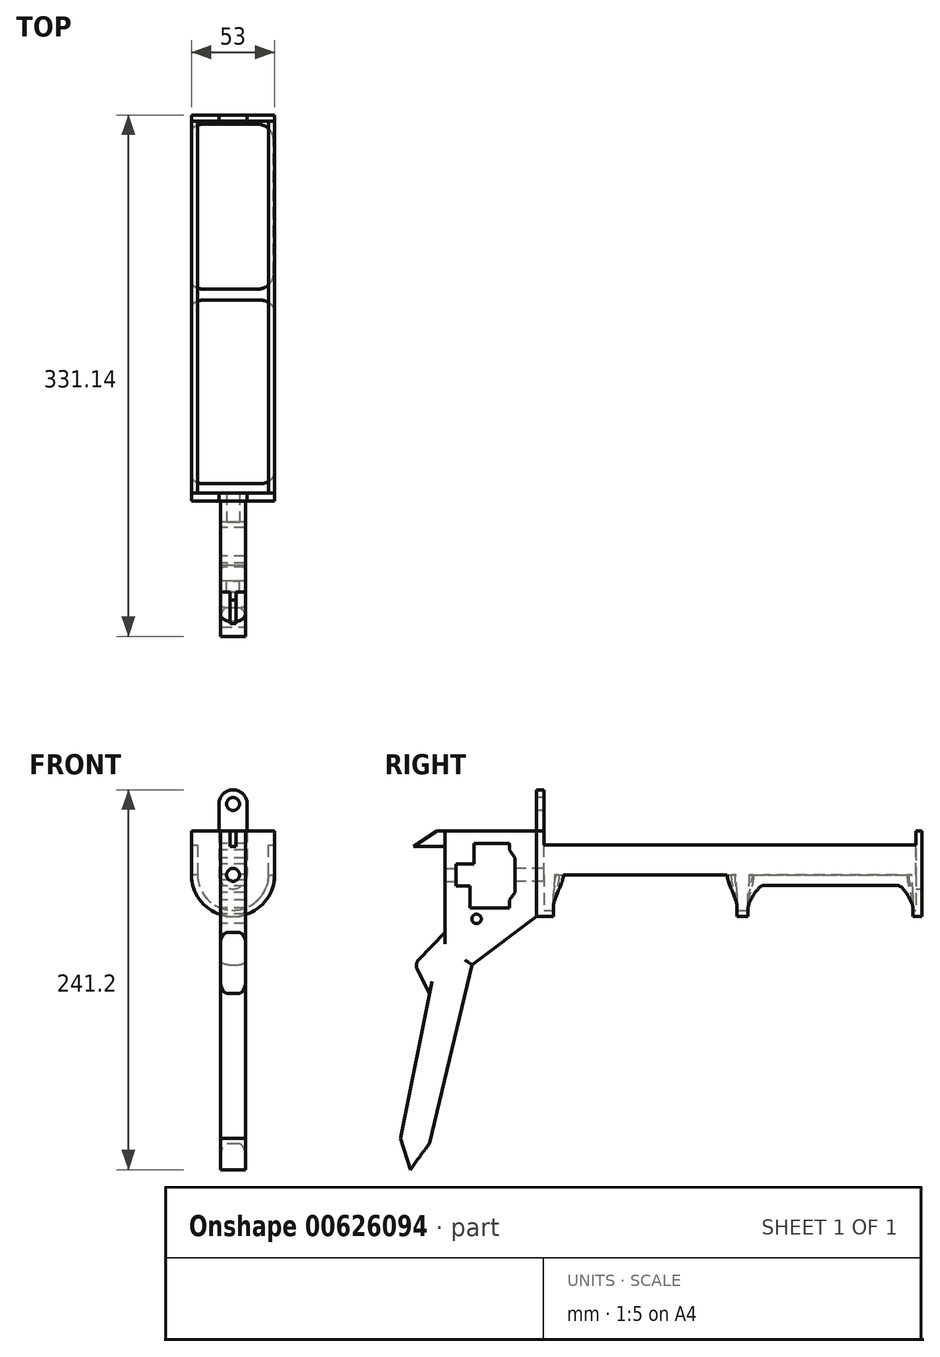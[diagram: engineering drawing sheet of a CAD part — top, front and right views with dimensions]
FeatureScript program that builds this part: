
annotation { "Feature Type Name" : "Feature", "Feature Type Description" : "" }
export const myFeature = defineFeature(function(context is Context, id is Id, definition is map)
    precondition{}
    {
        {
            var Q0;
            Q0=qCreatedBy(makeId("Front.planeOp"),FACE);
            var sketch = newSketch(context, id + "F0", { "sketchPlane" : qUnion([Q0])});
            skLineSegment(sketch, "E0", {"start": v(-22.5, 19) * mm, "end": v(-22.5, 0) * mm});
            skLineSegment(sketch, "E1", {"start": v(22.5, 0) * mm, "end": v(22.5, 19) * mm});
            skArc(sketch, "E2", {"start": v(-22.5, 0) * mm, "mid": v(0, -22.5) * mm, "end": v(22.5, 0) * mm});
            skLineSegment(sketch, "E3", {"start": v(-26.5, 19) * mm, "end": v(-26.5, 0) * mm});
            skLineSegment(sketch, "E4", {"start": v(26.5, 19) * mm, "end": v(26.5, 0) * mm});
            skArc(sketch, "E5", {"start": v(-26.5, 0) * mm, "mid": v(0, -26.5) * mm, "end": v(26.5, 0) * mm});
            skLineSegment(sketch, "E6", {"start": v(-26.5, 19) * mm, "end": v(-22.5, 19) * mm});
            skLineSegment(sketch, "E7", {"start": v(22.5, 19) * mm, "end": v(26.5, 19) * mm});
            skSolve(sketch);
        }
        {
            var Q0;
            Q0=makeQuery(id+"F0.imprint","IMPRINT",FACE,{"disambiguationData":[TD([[makeQuery(id+"F0.imprint","IMPRINT",EDGE,{"derivedFrom":sQuery(id+"F0.wireOp",EDGE,"E0")}),-1.0]])]});
            extrude(context, id + "F1", {"entities" : qUnion([Q0]), "depth" : 245 * mm, "offsetDistance" : 25 * mm});
        }
        {
            var Q0;
            Q0=qCreatedBy(makeId("Top.planeOp"),FACE);
            var sketch = newSketch(context, id + "F2", { "sketchPlane" : qUnion([Q0])});
            skLineSegment(sketch, "E8.bottom", {"start": v(-18.87, -5.77) * mm, "end": v(15.64, -5.77) * mm});
            skLineSegment(sketch, "E8.top", {"start": v(-18.87, -110.54) * mm, "end": v(15.64, -110.54) * mm});
            skLineSegment(sketch, "E8.left", {"start": v(-28.87, -15.77) * mm, "end": v(-28.87, -100.54) * mm});
            skLineSegment(sketch, "E8.right", {"start": v(25.64, -15.77) * mm, "end": v(25.64, -100.54) * mm});
            skLineSegment(sketch, "E9.bottom", {"start": v(-18.87, -117.53) * mm, "end": v(17.22, -117.53) * mm});
            skLineSegment(sketch, "E9.top", {"start": v(-18.87, -234.13) * mm, "end": v(17.22, -234.13) * mm});
            skLineSegment(sketch, "E9.left", {"start": v(-28.87, -127.53) * mm, "end": v(-28.87, -224.13) * mm});
            skLineSegment(sketch, "E9.right", {"start": v(27.22, -127.53) * mm, "end": v(27.22, -224.13) * mm});
            skPoint(sketch, "E10.visualSharp", {"position": v(-28.87, -117.53) * mm});
            skArc(sketch, "E10.filletArc", {"start": v(-18.87, -117.53) * mm, "mid": v(-25.94, -120.46) * mm, "end": v(-28.87, -127.53) * mm});
            skPoint(sketch, "E11.visualSharp", {"position": v(27.22, -117.53) * mm});
            skArc(sketch, "E11.filletArc", {"start": v(27.22, -127.53) * mm, "mid": v(24.3, -120.46) * mm, "end": v(17.22, -117.53) * mm});
            skPoint(sketch, "E12.visualSharp", {"position": v(-28.87, -234.13) * mm});
            skArc(sketch, "E12.filletArc", {"start": v(-28.87, -224.13) * mm, "mid": v(-25.94, -231.2) * mm, "end": v(-18.87, -234.13) * mm});
            skPoint(sketch, "E13.visualSharp", {"position": v(27.22, -234.13) * mm});
            skArc(sketch, "E13.filletArc", {"start": v(17.22, -234.13) * mm, "mid": v(24.3, -231.2) * mm, "end": v(27.22, -224.13) * mm});
            skPoint(sketch, "E14.visualSharp", {"position": v(-28.87, -110.54) * mm});
            skArc(sketch, "E14.filletArc", {"start": v(-28.87, -100.54) * mm, "mid": v(-25.94, -107.61) * mm, "end": v(-18.87, -110.54) * mm});
            skPoint(sketch, "E15.visualSharp", {"position": v(25.64, -110.54) * mm});
            skArc(sketch, "E15.filletArc", {"start": v(15.64, -110.54) * mm, "mid": v(22.72, -107.61) * mm, "end": v(25.64, -100.54) * mm});
            skPoint(sketch, "E16.visualSharp", {"position": v(25.64, -5.77) * mm});
            skArc(sketch, "E16.filletArc", {"start": v(25.64, -15.77) * mm, "mid": v(22.72, -8.7) * mm, "end": v(15.64, -5.77) * mm});
            skPoint(sketch, "E17.visualSharp", {"position": v(-28.87, -5.77) * mm});
            skArc(sketch, "E17.filletArc", {"start": v(-18.87, -5.77) * mm, "mid": v(-25.94, -8.7) * mm, "end": v(-28.87, -15.77) * mm});
            skSolve(sketch);
        }
        {
            var Q0;
            Q0=makeQuery(id+"F2.imprint","IMPRINT",FACE,{"disambiguationData":[TD([[makeQuery(id+"F2.imprint","IMPRINT",EDGE,{"derivedFrom":sQuery(id+"F2.wireOp",EDGE,"E9.bottom")}),-1.0]])]});
            var Q1;
            Q1=makeQuery(id+"F2.imprint","IMPRINT",FACE,{"disambiguationData":[TD([[makeQuery(id+"F2.imprint","IMPRINT",EDGE,{"derivedFrom":sQuery(id+"F2.wireOp",EDGE,"E8.bottom")}),-1.0]])]});
            extrude(context, id + "F3", {"entities" : qUnion([Q0, Q1]), "operationType" : NewBodyOperationType.REMOVE, "endBound" : BoundingType.THROUGH_ALL, "oppositeDirection" : true, "depth" : 25 * mm, "offsetDistance" : 25 * mm});
        }
        {
            var Q0;
            Q0=makeQuery(id+"F1.opExtrude","CAP_FACE",FACE,{"disambiguationData":[OSD([sQuery(id+"F0.wireOp",EDGE,"E0"),sQuery(id+"F0.wireOp",EDGE,"E1"),sQuery(id+"F0.wireOp",EDGE,"E2"),sQuery(id+"F0.wireOp",EDGE,"E3"),sQuery(id+"F0.wireOp",EDGE,"E4"),sQuery(id+"F0.wireOp",EDGE,"E5"),sQuery(id+"F0.wireOp",EDGE,"E6"),sQuery(id+"F0.wireOp",EDGE,"E7")])],"isStart":true});
            var sketch = newSketch(context, id + "F4", { "sketchPlane" : qUnion([Q0])});
            skLineSegment(sketch, "E18", {"start": v(-22.5, 19) * mm, "end": v(-8.92, 19) * mm});
            skLineSegment(sketch, "E19", {"start": v(-8.92, 19) * mm, "end": v(-8.92, 0) * mm});
            skLineSegment(sketch, "E20", {"start": v(22.5, 19) * mm, "end": v(8.92, 19) * mm});
            skLineSegment(sketch, "E21", {"start": v(8.92, 19) * mm, "end": v(8.92, 0) * mm});
            skArc(sketch, "E22", {"start": v(-8.92, 0) * mm, "mid": v(0, -8.92) * mm, "end": v(8.92, 0) * mm});
            skSolve(sketch);
        }
        {
            var Q0;
            Q0=makeQuery(id+"F4.imprint","IMPRINT",FACE,{"disambiguationData":[TD([[makeQuery(id+"F4.imprint","IMPRINT",EDGE,{"derivedFrom":sQuery(id+"F4.wireOp",EDGE,"E18")}),-1.0]])]});
            extrude(context, id + "F5", {"entities" : qUnion([Q0]), "operationType" : NewBodyOperationType.ADD, "oppositeDirection" : true, "depth" : 4 * mm, "offsetDistance" : 25 * mm});
        }
        {
            var Q0;
            Q0=makeQuery(id+"F1.opExtrude","CAP_FACE",FACE,{"disambiguationData":[OSD([sQuery(id+"F0.wireOp",EDGE,"E0"),sQuery(id+"F0.wireOp",EDGE,"E1"),sQuery(id+"F0.wireOp",EDGE,"E2"),sQuery(id+"F0.wireOp",EDGE,"E3"),sQuery(id+"F0.wireOp",EDGE,"E4"),sQuery(id+"F0.wireOp",EDGE,"E5"),sQuery(id+"F0.wireOp",EDGE,"E6"),sQuery(id+"F0.wireOp",EDGE,"E7")])],"isStart":false});
            var sketch = newSketch(context, id + "F6", { "sketchPlane" : qUnion([Q0])});
            skLineSegment(sketch, "E23", {"start": v(-26.5, 19) * mm, "end": v(-26.5, 28) * mm});
            skLineSegment(sketch, "E24", {"start": v(-26.5, 28) * mm, "end": v(-8.92, 28) * mm});
            skLineSegment(sketch, "E25", {"start": v(26.5, 19) * mm, "end": v(26.5, 28) * mm});
            skLineSegment(sketch, "E26", {"start": v(26.5, 28) * mm, "end": v(8.92, 28) * mm});
            skLineSegment(sketch, "E27", {"start": v(8.92, 28) * mm, "end": v(8.92, 45) * mm});
            skLineSegment(sketch, "E28", {"start": v(-8.92, 28) * mm, "end": v(-8.92, 45) * mm});
            skArc(sketch, "E29", {"start": v(8.92, 45) * mm, "mid": v(0, 53.92) * mm, "end": v(-8.92, 45) * mm});
            skSolve(sketch);
        }
        {
            var Q0;
            Q0=makeQuery(id+"F6.imprint","IMPRINT",FACE,{"disambiguationData":[TD([[makeQuery(id+"F6.imprint","IMPRINT",EDGE,{"derivedFrom":sQuery(id+"F6.wireOp",EDGE,"E23")}),-1.0]])]});
            extrude(context, id + "F7", {"entities" : qUnion([Q0]), "operationType" : NewBodyOperationType.ADD, "oppositeDirection" : true, "depth" : 4.8 * mm, "offsetDistance" : 25 * mm});
        }
        {
            var Q0;
            {var subQ0=sQuery(id+"F0.wireOp",EDGE,"E7");var subQ1=sQuery(id+"F0.wireOp",EDGE,"E6");var subQ2=sQuery(id+"F0.wireOp",EDGE,"E2");var subQ3=sQuery(id+"F0.wireOp",EDGE,"E1");var subQ4=sQuery(id+"F0.wireOp",EDGE,"E0");Q0=makeQuery(id+"F7.boolean.opBoolean","MERGE",FACE,{"derivedFrom":[makeQuery(id+"F1.opExtrude","CAP_FACE",FACE,{"disambiguationData":[OSD([subQ4,subQ3,subQ2,sQuery(id+"F0.wireOp",EDGE,"E3"),sQuery(id+"F0.wireOp",EDGE,"E4"),sQuery(id+"F0.wireOp",EDGE,"E5"),subQ1,subQ0])],"isStart":false}),makeQuery(id+"F7.opExtrude","CAP_FACE",FACE,{"disambiguationData":[OSD([subQ4,subQ3,subQ2,subQ1,subQ0,sQuery(id+"F6.wireOp",EDGE,"E23"),sQuery(id+"F6.wireOp",EDGE,"E24"),sQuery(id+"F6.wireOp",EDGE,"E25"),sQuery(id+"F6.wireOp",EDGE,"E26"),sQuery(id+"F6.wireOp",EDGE,"E27"),sQuery(id+"F6.wireOp",EDGE,"E28"),sQuery(id+"F6.wireOp",EDGE,"E29")])],"isStart":true})]});}
            var sketch = newSketch(context, id + "F8", { "sketchPlane" : qUnion([Q0])});
            skCircle(sketch, "E30", {"center": v(0, 45) * mm, "radius": 4.1 * mm});
            skCircle(sketch, "E31", {"center": v(0, 0) * mm, "radius": 4.1 * mm});
            skSolve(sketch);
        }
        {
            var Q0;
            Q0=makeQuery(id+"F8.imprint","IMPRINT",FACE,{"disambiguationData":[TD([[makeQuery(id+"F8.imprint","IMPRINT",EDGE,{"derivedFrom":sQuery(id+"F8.wireOp",EDGE,"E30")}),1.0]])]});
            var Q1;
            Q1=makeQuery(id+"F8.imprint","IMPRINT",FACE,{"disambiguationData":[TD([[makeQuery(id+"F8.imprint","IMPRINT",EDGE,{"derivedFrom":sQuery(id+"F8.wireOp",EDGE,"E31")}),1.0]])]});
            extrude(context, id + "F9", {"entities" : qUnion([Q0, Q1]), "operationType" : NewBodyOperationType.REMOVE, "endBound" : BoundingType.THROUGH_ALL, "oppositeDirection" : true, "depth" : 25 * mm, "offsetDistance" : 25 * mm});
        }
        {
            var Q0;
            {var subQ0=sQuery(id+"F0.wireOp",EDGE,"E2");var subQ1=sQuery(id+"F0.wireOp",EDGE,"E1");var subQ2=sQuery(id+"F0.wireOp",EDGE,"E0");Q0=makeQuery(id+"F5.boolean.opBoolean","MERGE",FACE,{"derivedFrom":[makeQuery(id+"F1.opExtrude","CAP_FACE",FACE,{"disambiguationData":[OSD([subQ2,subQ1,subQ0,sQuery(id+"F0.wireOp",EDGE,"E3"),sQuery(id+"F0.wireOp",EDGE,"E4"),sQuery(id+"F0.wireOp",EDGE,"E5"),sQuery(id+"F0.wireOp",EDGE,"E6"),sQuery(id+"F0.wireOp",EDGE,"E7")])],"isStart":true}),makeQuery(id+"F5.opExtrude","CAP_FACE",FACE,{"disambiguationData":[OSD([subQ2,subQ1,subQ0,sQuery(id+"F4.wireOp",EDGE,"E18"),sQuery(id+"F4.wireOp",EDGE,"E19"),sQuery(id+"F4.wireOp",EDGE,"E20"),sQuery(id+"F4.wireOp",EDGE,"E21"),sQuery(id+"F4.wireOp",EDGE,"E22")])],"isStart":true})]});}
            var sketch = newSketch(context, id + "F10", { "sketchPlane" : qUnion([Q0])});
            skLineSegment(sketch, "E32", {"start": v(-26.5, 19) * mm, "end": v(-26.5, 28) * mm});
            skLineSegment(sketch, "E33", {"start": v(-26.5, 28) * mm, "end": v(-8.92, 28) * mm});
            skLineSegment(sketch, "E34", {"start": v(26.5, 19) * mm, "end": v(26.5, 28) * mm});
            skLineSegment(sketch, "E35", {"start": v(26.5, 28) * mm, "end": v(8.92, 28) * mm});
            skLineSegment(sketch, "E36", {"start": v(-8.92, 28) * mm, "end": v(-8.92, 19) * mm});
            skLineSegment(sketch, "E37", {"start": v(8.92, 28) * mm, "end": v(8.92, 19) * mm});
            skSolve(sketch);
        }
        {
            var Q0;
            Q0=makeQuery(id+"F10.imprint","IMPRINT",FACE,{"disambiguationData":[TD([[makeQuery(id+"F10.imprint","IMPRINT",EDGE,{"derivedFrom":sQuery(id+"F10.wireOp",EDGE,"E32")}),-1.0]])]});
            var Q1;
            Q1=makeQuery(id+"F10.imprint","IMPRINT",FACE,{"disambiguationData":[TD([[makeQuery(id+"F10.imprint","IMPRINT",EDGE,{"derivedFrom":sQuery(id+"F10.wireOp",EDGE,"E34")}),1.0]])]});
            extrude(context, id + "F11", {"entities" : qUnion([Q0, Q1]), "operationType" : NewBodyOperationType.ADD, "oppositeDirection" : true, "depth" : 4 * mm, "offsetDistance" : 25 * mm});
        }
        {
            var Q0;
            Q0=makeQuery(id+"F11.boolean.opBoolean","MERGE",FACE,{"derivedFrom":[makeQuery(id+"F7.boolean.opBoolean","MERGE",FACE,{"derivedFrom":[makeQuery(id+"F1.opExtrude","SWEPT_FACE",FACE,{"disambiguationData":[OSD([sQuery(id+"F0.wireOp",EDGE,"E3")])]}),makeQuery(id+"F7.opExtrude","SWEPT_FACE",FACE,{"disambiguationData":[OSD([sQuery(id+"F6.wireOp",EDGE,"E23")])]})]}),makeQuery(id+"F11.opExtrude","SWEPT_FACE",FACE,{"disambiguationData":[OSD([sQuery(id+"F10.wireOp",EDGE,"E34")])]})]});
            cPlane(context, id + "F12", {"entities" : qUnion([Q0]), "cplaneType" : CPlaneType.OFFSET, "offset" : 26.5 * mm, "oppositeDirection" : true, "width" : 150 * mm, "height" : 150 * mm});
        }
        {
            var Q0;
            Q0=qCreatedBy(id+"F12.planeOp",FACE);
            var sketch = newSketch(context, id + "F13", { "sketchPlane" : qUnion([Q0])});
            skLineSegment(sketch, "E38", {"start": v(245, -26.5) * mm, "end": v(285.8, -57.1) * mm});
            skLineSegment(sketch, "E39", {"start": v(285.8, -57.1) * mm, "end": v(312.75, -170.44) * mm});
            skLineSegment(sketch, "E40", {"start": v(312.75, -75.45) * mm, "end": v(322.32, -56.75) * mm});
            skLineSegment(sketch, "E41", {"start": v(322.32, -56.75) * mm, "end": v(302.98, -36.5) * mm});
            skLineSegment(sketch, "E42", {"start": v(302.98, -36.5) * mm, "end": v(302.98, 28) * mm});
            skLineSegment(sketch, "E43", {"start": v(245, 28) * mm, "end": v(245, -26.5) * mm});
            skLineSegment(sketch, "E44", {"start": v(312.75, -75.45) * mm, "end": v(331.14, -167.3) * mm});
            skLineSegment(sketch, "E45", {"start": v(331.14, -167.3) * mm, "end": v(325.09, -187.28) * mm});
            skLineSegment(sketch, "E46", {"start": v(325.09, -187.28) * mm, "end": v(312.75, -170.44) * mm});
            skLineSegment(sketch, "E47", {"start": v(245, 28) * mm, "end": v(302.98, 28) * mm});
            skLineSegment(sketch, "E48", {"start": v(302.98, 28) * mm, "end": v(307.98, 28) * mm});
            skLineSegment(sketch, "E49", {"start": v(307.98, 28) * mm, "end": v(322.98, 18) * mm});
            skLineSegment(sketch, "E50", {"start": v(322.98, 18) * mm, "end": v(302.98, 18) * mm});
            skSolve(sketch);
        }
        {
            var Q0;
            Q0=makeQuery(id+"F13.imprint","IMPRINT",FACE,{"disambiguationData":[TD([[makeQuery(id+"F13.imprint","IMPRINT",EDGE,{"derivedFrom":sQuery(id+"F13.wireOp",EDGE,"E38")}),1.0]])]});
            extrude(context, id + "F14", {"entities" : qUnion([Q0]), "operationType" : NewBodyOperationType.ADD, "depth" : 16 * mm, "offsetDistance" : 25 * mm, "symmetric" : true});
        }
        {
            var Q0;
            Q0=makeQuery(id+"F14.opExtrude","CAP_FACE",FACE,{"disambiguationData":[OSD([sQuery(id+"F13.wireOp",EDGE,"E38"),sQuery(id+"F13.wireOp",EDGE,"E39"),sQuery(id+"F13.wireOp",EDGE,"a49a05dd-48e7-42bd-a879-3531206f20a7"),sQuery(id+"F13.wireOp",EDGE,"E40"),sQuery(id+"F13.wireOp",EDGE,"E41"),sQuery(id+"F13.wireOp",EDGE,"E42"),sQuery(id+"F13.wireOp",EDGE,"HMM0x2BH-GEp6-wL4u-TX3u-38hgBbOKYSqe"),sQuery(id+"F13.wireOp",EDGE,"E43")])],"isStart":false});
            var sketch = newSketch(context, id + "F15", { "sketchPlane" : qUnion([Q0])});
            skLineSegment(sketch, "E51", {"start": v(262, 20) * mm, "end": v(262, 15.74) * mm});
            skLineSegment(sketch, "E52", {"start": v(262, 15.74) * mm, "end": v(258.5, 10.87) * mm});
            skLineSegment(sketch, "E53", {"start": v(258.5, 10.87) * mm, "end": v(258.5, -11.13) * mm});
            skLineSegment(sketch, "E54", {"start": v(258.5, -11.13) * mm, "end": v(262, -16) * mm});
            skLineSegment(sketch, "E55", {"start": v(262, -16) * mm, "end": v(262, -21) * mm});
            skLineSegment(sketch, "E56", {"start": v(262, -21) * mm, "end": v(287, -21) * mm});
            skLineSegment(sketch, "E57", {"start": v(287, -21) * mm, "end": v(287, -7) * mm});
            skLineSegment(sketch, "E58", {"start": v(287, -7) * mm, "end": v(295.98, -7) * mm});
            skLineSegment(sketch, "E59", {"start": v(295.98, -7) * mm, "end": v(295.98, 7) * mm});
            skLineSegment(sketch, "E60", {"start": v(295.98, 7) * mm, "end": v(284.48, 7) * mm});
            skLineSegment(sketch, "E61", {"start": v(284.48, 7) * mm, "end": v(284.48, 20) * mm});
            skLineSegment(sketch, "E62", {"start": v(284.48, 20) * mm, "end": v(262, 20) * mm});
            skLineSegment(sketch, "E63", {"start": v(258.5, -3.3) * mm, "end": v(258.5, -3.3) * mm});
            skLineSegment(sketch, "E64", {"start": v(258.5, -3.3) * mm, "end": v(258.5, 0.14) * mm});
            skLineSegment(sketch, "E65", {"start": v(258.5, 0.14) * mm, "end": v(258.5, 0.14) * mm});
            skSolve(sketch);
        }
        {
            var Q0;
            Q0=makeQuery(id+"F15.imprint","IMPRINT",FACE,{"disambiguationData":[TD([[makeQuery(id+"F15.imprint","IMPRINT",EDGE,{"derivedFrom":sQuery(id+"F15.wireOp",EDGE,"E51")}),1.0]])]});
            extrude(context, id + "F16", {"entities" : qUnion([Q0]), "operationType" : NewBodyOperationType.REMOVE, "endBound" : BoundingType.THROUGH_ALL, "oppositeDirection" : true, "depth" : 25 * mm, "offsetDistance" : 25 * mm});
        }
        {
            var Q0;
            Q0=makeQuery(id+"F14.boolean.opBoolean","SPLIT",FACE,{"disambiguationData":[TD([makeQuery(id+"F9.boolean.opBoolean","COPY",FACE,{"derivedFrom":makeQuery(id+"F9.opExtrude","SWEPT_FACE",FACE,{"disambiguationData":[OSD([sQuery(id+"F8.wireOp",EDGE,"E31")])]})})])],"derivedFrom":makeQuery(id+"F14.opExtrude","SWEPT_FACE",FACE,{"disambiguationData":[OSD([sQuery(id+"F13.wireOp",EDGE,"E43")])]})});
            extrude(context, id + "F17", {"entities" : qUnion([Q0]), "operationType" : NewBodyOperationType.REMOVE, "endBound" : BoundingType.THROUGH_ALL, "oppositeDirection" : true, "depth" : 25 * mm, "offsetDistance" : 25 * mm});
        }
        {
            var Q0;
            Q0=makeQuery(id+"F14.opExtrude","CAP_FACE",FACE,{"disambiguationData":[OSD([sQuery(id+"F13.wireOp",EDGE,"E38"),sQuery(id+"F13.wireOp",EDGE,"E39"),sQuery(id+"F13.wireOp",EDGE,"a49a05dd-48e7-42bd-a879-3531206f20a7"),sQuery(id+"F13.wireOp",EDGE,"E40"),sQuery(id+"F13.wireOp",EDGE,"E41"),sQuery(id+"F13.wireOp",EDGE,"E42"),sQuery(id+"F13.wireOp",EDGE,"HMM0x2BH-GEp6-wL4u-TX3u-38hgBbOKYSqe"),sQuery(id+"F13.wireOp",EDGE,"E43")])],"isStart":false});
            var sketch = newSketch(context, id + "F18", { "sketchPlane" : qUnion([Q0])});
            skCircle(sketch, "E66", {"center": v(282.98, -28) * mm, "radius": 3 * mm});
            skSolve(sketch);
        }
        {
            var Q0;
            Q0 = qSketchRegion(id + "F18", true);
            extrude(context, id + "F19", {"entities" : qUnion([Q0]), "operationType" : NewBodyOperationType.REMOVE, "oppositeDirection" : true, "depth" : 25 * mm, "offsetDistance" : 25 * mm});
        }
        {
            var Q0;
            Q0=makeQuery(id+"F14.opExtrude","SWEPT_EDGE",EDGE,{"disambiguationData":[OSD([sQuery(id+"F13.wireOp",EDGE,"E40"),sQuery(id+"F13.wireOp",EDGE,"E41")])]});
            fillet(context, id + "F20", {"entities" : qUnion([Q0]), "radius" : 5 * mm, "tangentPropagation" : true, "defaultsChanged" : false, "allowEdgeOverflow" : false, "vertexSettings" : [], "filletType" : FilletType.EDGE});
        }
        {
            var Q0;
            Q0=makeQuery(id+"F14.opExtrude","CAP_EDGE",EDGE,{"disambiguationData":[OSD([sQuery(id+"F13.wireOp",EDGE,"HMM0x2BH-GEp6-wL4u-TX3u-38hgBbOKYSqe")])],"isStart":false});
            var Q1;
            Q1=makeQuery(id+"F14.opExtrude","CAP_EDGE",EDGE,{"disambiguationData":[OSD([sQuery(id+"F13.wireOp",EDGE,"HMM0x2BH-GEp6-wL4u-TX3u-38hgBbOKYSqe")])],"isStart":true});
            var Q2;
            Q2=makeQuery(id+"F14.opExtrude","CAP_EDGE",EDGE,{"disambiguationData":[OSD([sQuery(id+"F13.wireOp",EDGE,"E41")])],"isStart":false});
            var Q3;
            Q3=makeQuery(id+"F14.opExtrude","CAP_EDGE",EDGE,{"disambiguationData":[OSD([sQuery(id+"F13.wireOp",EDGE,"E41")])],"isStart":true});
            var Q4;
            Q4=makeQuery(id+"F14.opExtrude","CAP_EDGE",EDGE,{"disambiguationData":[OSD([sQuery(id+"F13.wireOp",EDGE,"a49a05dd-48e7-42bd-a879-3531206f20a7")])],"isStart":false});
            var Q5;
            Q5=makeQuery(id+"F14.opExtrude","CAP_EDGE",EDGE,{"disambiguationData":[OSD([sQuery(id+"F13.wireOp",EDGE,"E39")])],"isStart":false});
            var Q6;
            Q6=makeQuery(id+"F14.opExtrude","CAP_EDGE",EDGE,{"disambiguationData":[OSD([sQuery(id+"F13.wireOp",EDGE,"E38")])],"isStart":false});
            var Q7;
            Q7=makeQuery(id+"F14.opExtrude","CAP_EDGE",EDGE,{"disambiguationData":[OSD([sQuery(id+"F13.wireOp",EDGE,"a49a05dd-48e7-42bd-a879-3531206f20a7")])],"isStart":true});
            var Q8;
            Q8=makeQuery(id+"F14.opExtrude","CAP_EDGE",EDGE,{"disambiguationData":[OSD([sQuery(id+"F13.wireOp",EDGE,"E39")])],"isStart":true});
            var Q9;
            Q9=makeQuery(id+"F14.opExtrude","CAP_EDGE",EDGE,{"disambiguationData":[OSD([sQuery(id+"F13.wireOp",EDGE,"E38")])],"isStart":true});
            fillet(context, id + "F21", {"entities" : qUnion([Q0, Q1, Q2, Q3, Q4, Q5, Q6, Q7, Q8, Q9]), "radius" : 5 * mm, "tangentPropagation" : true, "allowEdgeOverflow" : false});
        }
        {
            var Q0;
            {var subQ0=sQuery(id+"F13.wireOp",EDGE,"E48");Q0=makeQuery(id+"F13.imprint","IMPRINT",FACE,{"disambiguationData":[TD([[makeQuery(id+"F13.imprint","IMPRINT",EDGE,{"derivedFrom":subQ0}),-1.0]])]});}
            extrude(context, id + "F22", {"entities" : qUnion([Q0]), "operationType" : NewBodyOperationType.ADD, "depth" : 4 * mm, "offsetDistance" : 25 * mm, "symmetric" : true});
        }
    });
